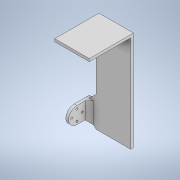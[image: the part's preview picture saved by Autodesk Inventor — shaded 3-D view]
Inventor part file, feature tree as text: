
AUTODESK INVENTOR PART (.ipt)
format: ipt  version: 2020 (Build 240168000, 168)  size: 212,992 bytes
history: native  units: in
note: dims shown in document units (in); Inventor stores cm internally (conversion verified against a paired STEP export)
features: extrude x6, sketch x6, chamfer x3
ambient origin geometry x8: Origin, YZ Plane, XZ Plane, XY Plane, X Axis, Y Axis, Z Axis, Center Point
bodies: Solid1 (feature_tree)
feature tree (15):
  extrude  "Extrusion1"  Depth=1.2in
  extrude  "Extrusion3"  Depth=0.1406in
  extrude  "Extrusion4"  Depth=0.1406in
  extrude  "Extrusion5"  Depth=0.2in
  chamfer  "Chamfer1"  Distance=0.2in
  chamfer  "Chamfer2"  Distance=0.5in
  chamfer  "Chamfer3"  Distance=2.5in
  extrude  "Extrusion6"  Depth=6.5in
  extrude  "Extrusion7"  Depth=0.5in
  sketch  "Sketch1"  dims[d0=1.2in d1=0.77in]
  sketch  "Sketch5"  dims[d2=0.1406in d3=0.1406in]
  sketch  "Sketch6"  dims[d4=0.1406in d5=0.1406in]
  sketch  "Sketch7"  dims[d7=0.2in d8=0.0in d17=1.1in]
  sketch  "Sketch9"  dims[d18=1.2in d19=0.2in d20=0.0in]
  sketch  "Sketch10"  dims[d21=0.2in d22=0.5in d23=0.0in d24=2.5in d25=6.5in d26=0.5in d27=0.2in d28=0.0in d30=0.3125in d31=0.125in d32=45.0deg d33=0.5in d34=0.125in d35=45.0deg d36=0.5in d37=0.125in d38=45.0deg d47=0.25in d48=6.7in d49=0.25in d50=0.25in d51=0.5in d52=0.5in d53=0.1in d54=0.0in d55=2.5in d56=0.2in d57=3.2in d58=0.0in]
